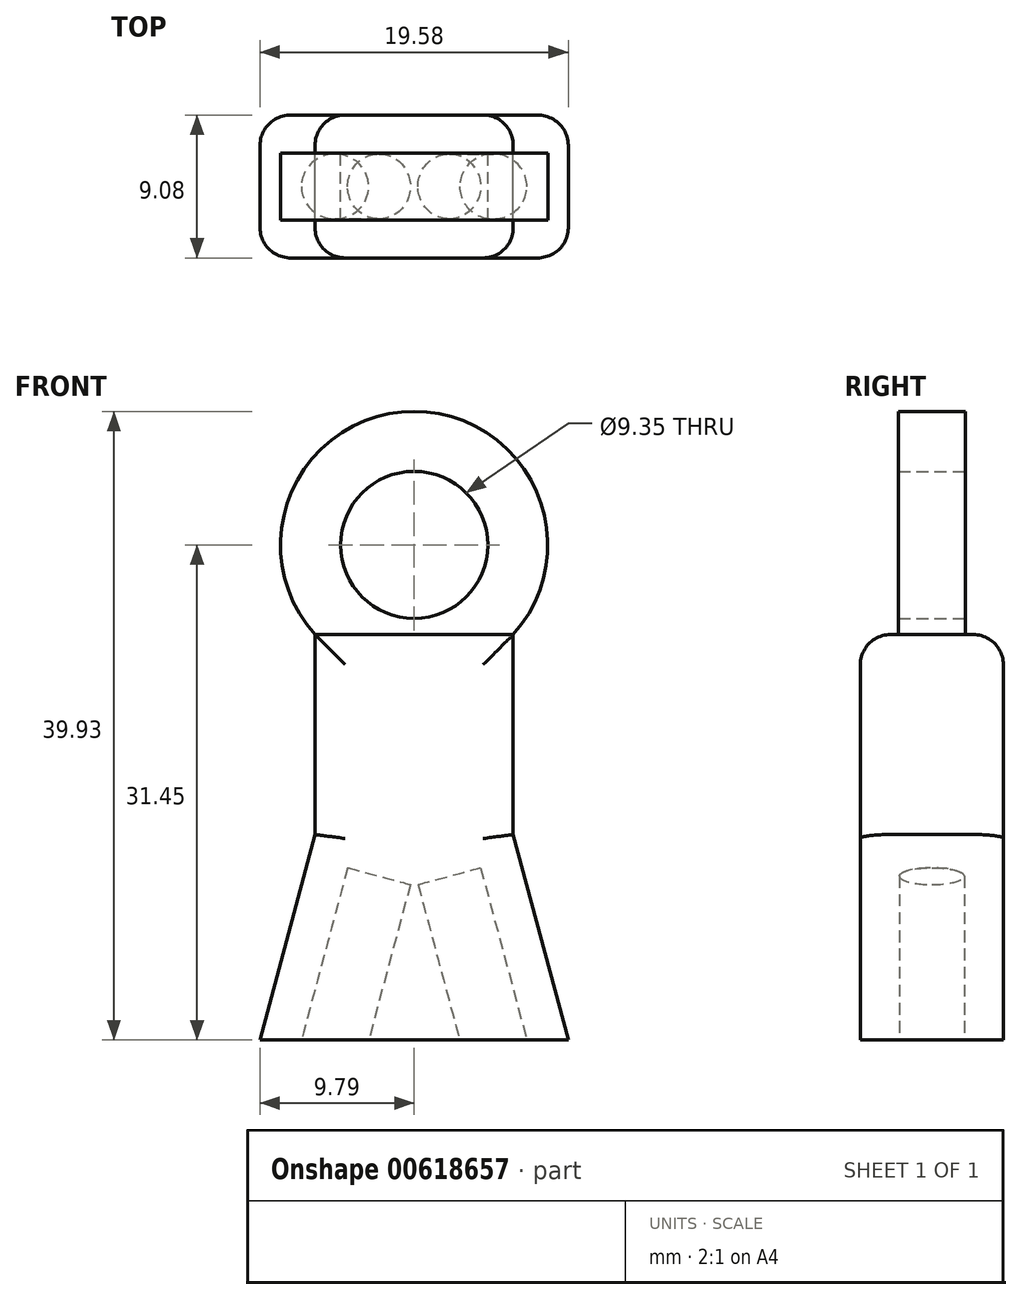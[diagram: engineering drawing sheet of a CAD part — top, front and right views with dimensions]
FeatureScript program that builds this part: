
annotation { "Feature Type Name" : "Feature", "Feature Type Description" : "" }
export const myFeature = defineFeature(function(context is Context, id is Id, definition is map)
    precondition{}
    {
        {
            var Q0;
            Q0=qCreatedBy(makeId("Front.planeOp"),FACE);
            var sketch = newSketch(context, id + "F0", { "sketchPlane" : qUnion([Q0])});
            skCircle(sketch, "E0", {"center": v(0, 0) * mm, "radius": 4.68 * mm});
            skCircle(sketch, "E1", {"center": v(0, 0) * mm, "radius": 8.48 * mm});
            skSolve(sketch);
        }
        {
            var Q0;
            Q0=qSketchRegion(id+"F0",true);
            extrude(context, id + "F1", {"entities" : qUnion([Q0]), "endBound" : BoundingType.SYMMETRIC, "depth" : 4.25 * mm, "offsetDistance" : 25.4 * mm});
        }
        {
            var Q0;
            Q0=qCreatedBy(makeId("Front.planeOp"),FACE);
            var sketch = newSketch(context, id + "F2", { "sketchPlane" : qUnion([Q0])});
            skLineSegment(sketch, "E2", {"start": v(0, -12.7) * mm, "end": v(-5.35, -32.65) * mm, "construction": true});
            skLineSegment(sketch, "E3", {"start": v(0, -12.7) * mm, "end": v(6.2, -35.83) * mm, "construction": true});
            skLineSegment(sketch, "E4", {"start": v(0, -12.7) * mm, "end": v(0, -24.9) * mm, "construction": true});
            skLineSegment(sketch, "E5", {"start": v(-4.23, -20.5) * mm, "end": v(0, -21.63) * mm, "construction": true});
            skLineSegment(sketch, "E6", {"start": v(0, -21.63) * mm, "end": v(4.23, -20.5) * mm, "construction": true});
            skLineSegment(sketch, "E7", {"start": v(-4.23, -20.5) * mm, "end": v(-6.86, -30.32) * mm, "construction": true});
            skLineSegment(sketch, "E8", {"start": v(0, -21.63) * mm, "end": v(-2.63, -31.45) * mm, "construction": true});
            skLineSegment(sketch, "E9", {"start": v(-9.79, -31.45) * mm, "end": v(9.79, -31.45) * mm});
            skLineSegment(sketch, "E10", {"start": v(-9.79, -31.45) * mm, "end": v(-6.3, -18.4) * mm});
            skLineSegment(sketch, "E11", {"start": v(-6.3, -18.4) * mm, "end": v(6.3, -18.4) * mm});
            skLineSegment(sketch, "E12", {"start": v(6.3, -18.4) * mm, "end": v(9.79, -31.45) * mm});
            skLineSegment(sketch, "E13.top", {"start": v(-6.3, -5.7) * mm, "end": v(6.3, -5.7) * mm});
            skLineSegment(sketch, "E13.left", {"start": v(-6.3, -18.4) * mm, "end": v(-6.3, -5.7) * mm});
            skLineSegment(sketch, "E13.right", {"start": v(6.3, -18.4) * mm, "end": v(6.3, -5.7) * mm});
            skSolve(sketch);
        }
        {
            var Q0;
            Q0=qSketchRegion(id+"F2",true);
            extrude(context, id + "F3", {"entities" : qUnion([Q0]), "operationType" : NewBodyOperationType.ADD, "endBound" : BoundingType.SYMMETRIC, "depth" : 9.08 * mm, "offsetDistance" : 25.4 * mm});
        }
        {
            var Q0;
            Q0=qCreatedBy(makeId("Front.planeOp"),FACE);
            var sketch = newSketch(context, id + "F4", { "sketchPlane" : qUnion([Q0])});
            skLineSegment(sketch, "E14.0", {"start": v(-4.23, -20.5) * mm, "end": v(0, -21.63) * mm});
            skLineSegment(sketch, "E15.0", {"start": v(-4.23, -20.5) * mm, "end": v(-6.86, -30.32) * mm});
            skLineSegment(sketch, "E16.0", {"start": v(0, -21.63) * mm, "end": v(4.23, -20.5) * mm});
            skLineSegment(sketch, "E17", {"start": v(-6.86, -30.32) * mm, "end": v(-7.16, -31.45) * mm});
            skLineSegment(sketch, "E18", {"start": v(-0.24, -21.57) * mm, "end": v(-2.89, -31.45) * mm});
            skLineSegment(sketch, "E19", {"start": v(-2.89, -31.45) * mm, "end": v(-7.16, -31.45) * mm});
            skLineSegment(sketch, "E20", {"start": v(4.23, -20.5) * mm, "end": v(7.16, -31.45) * mm});
            skLineSegment(sketch, "E21", {"start": v(0.24, -21.57) * mm, "end": v(2.89, -31.45) * mm});
            skLineSegment(sketch, "E22", {"start": v(2.89, -31.45) * mm, "end": v(7.16, -31.45) * mm});
            skSolve(sketch);
        }
        {
            var Q0;
            Q0=qSketchRegion(id+"F4",true);
            extrude(context, id + "F5", {"entities" : qUnion([Q0]), "operationType" : NewBodyOperationType.REMOVE, "endBound" : BoundingType.SYMMETRIC, "oppositeDirection" : true, "depth" : 4.12 * mm, "offsetDistance" : 25.4 * mm});
        }
        {
            var Q0;
            Q0=makeQuery(id+"F5.boolean.opBoolean","COPY",EDGE,{"derivedFrom":makeQuery(id+"F5.opExtrude","CAP_EDGE",EDGE,{"disambiguationData":[OSD([sQuery(id+"F4.wireOp",EDGE,"E15.0"),sQuery(id+"F4.wireOp",EDGE,"E17")])],"isStart":true})});
            var Q1;
            Q1=makeQuery(id+"F5.boolean.opBoolean","COPY",EDGE,{"derivedFrom":makeQuery(id+"F5.opExtrude","CAP_EDGE",EDGE,{"disambiguationData":[OSD([sQuery(id+"F4.wireOp",EDGE,"E21")])],"isStart":true})});
            var Q2;
            Q2=makeQuery(id+"F5.boolean.opBoolean","COPY",EDGE,{"derivedFrom":makeQuery(id+"F5.opExtrude","CAP_EDGE",EDGE,{"disambiguationData":[OSD([sQuery(id+"F4.wireOp",EDGE,"E20")])],"isStart":true})});
            var Q3;
            Q3=makeQuery(id+"F5.boolean.opBoolean","COPY",EDGE,{"derivedFrom":makeQuery(id+"F5.opExtrude","CAP_EDGE",EDGE,{"disambiguationData":[OSD([sQuery(id+"F4.wireOp",EDGE,"E18")])],"isStart":true})});
            var Q4;
            Q4=makeQuery(id+"F5.boolean.opBoolean","COPY",EDGE,{"derivedFrom":makeQuery(id+"F5.opExtrude","CAP_EDGE",EDGE,{"disambiguationData":[OSD([sQuery(id+"F4.wireOp",EDGE,"E20")])],"isStart":false})});
            var Q5;
            Q5=makeQuery(id+"F5.boolean.opBoolean","COPY",EDGE,{"derivedFrom":makeQuery(id+"F5.opExtrude","CAP_EDGE",EDGE,{"disambiguationData":[OSD([sQuery(id+"F4.wireOp",EDGE,"E18")])],"isStart":false})});
            var Q6;
            Q6=makeQuery(id+"F5.boolean.opBoolean","COPY",EDGE,{"derivedFrom":makeQuery(id+"F5.opExtrude","CAP_EDGE",EDGE,{"disambiguationData":[OSD([sQuery(id+"F4.wireOp",EDGE,"E15.0"),sQuery(id+"F4.wireOp",EDGE,"E17")])],"isStart":false})});
            var Q7;
            Q7=makeQuery(id+"F5.boolean.opBoolean","COPY",EDGE,{"derivedFrom":makeQuery(id+"F5.opExtrude","CAP_EDGE",EDGE,{"disambiguationData":[OSD([sQuery(id+"F4.wireOp",EDGE,"E21")])],"isStart":false})});
            fillet(context, id + "F6", {"entities" : qUnion([Q0, Q1, Q2, Q3, Q4, Q5, Q6, Q7]), "radius" : 4.12 * mm / 2, "tangentPropagation" : true, "allowEdgeOverflow" : false});
        }
        {
            var Q0;
            Q0=makeQuery(id+"F3.opExtrude","CAP_EDGE",EDGE,{"disambiguationData":[OSD([sQuery(id+"F2.wireOp",EDGE,"E10")])],"isStart":false});
            var Q1;
            Q1=makeQuery(id+"F3.opExtrude","CAP_EDGE",EDGE,{"disambiguationData":[OSD([sQuery(id+"F2.wireOp",EDGE,"E13.left")])],"isStart":false});
            var Q2;
            Q2=makeQuery(id+"F3.opExtrude","CAP_EDGE",EDGE,{"disambiguationData":[OSD([sQuery(id+"F2.wireOp",EDGE,"E13.left")])],"isStart":true});
            var Q3;
            Q3=makeQuery(id+"F3.opExtrude","CAP_EDGE",EDGE,{"disambiguationData":[OSD([sQuery(id+"F2.wireOp",EDGE,"E10")])],"isStart":true});
            var Q4;
            Q4=makeQuery(id+"F3.opExtrude","CAP_EDGE",EDGE,{"disambiguationData":[OSD([sQuery(id+"F2.wireOp",EDGE,"E12")])],"isStart":false});
            var Q5;
            Q5=makeQuery(id+"F3.opExtrude","CAP_EDGE",EDGE,{"disambiguationData":[OSD([sQuery(id+"F2.wireOp",EDGE,"E13.right")])],"isStart":false});
            var Q6;
            Q6=makeQuery(id+"F3.opExtrude","CAP_EDGE",EDGE,{"disambiguationData":[OSD([sQuery(id+"F2.wireOp",EDGE,"E12")])],"isStart":true});
            var Q7;
            Q7=makeQuery(id+"F3.opExtrude","CAP_EDGE",EDGE,{"disambiguationData":[OSD([sQuery(id+"F2.wireOp",EDGE,"E13.right")])],"isStart":true});
            var Q8;
            Q8=makeQuery(id+"F3.opExtrude","CAP_EDGE",EDGE,{"disambiguationData":[OSD([sQuery(id+"F2.wireOp",EDGE,"E13.top")])],"isStart":true});
            var Q9;
            Q9=makeQuery(id+"F3.opExtrude","CAP_EDGE",EDGE,{"disambiguationData":[OSD([sQuery(id+"F2.wireOp",EDGE,"E13.top")])],"isStart":false});
            fillet(context, id + "F7", {"entities" : qUnion([Q0, Q1, Q2, Q3, Q4, Q5, Q6, Q7, Q8, Q9]), "radius" : 1.9 * mm, "tangentPropagation" : true, "allowEdgeOverflow" : false});
        }
    });
